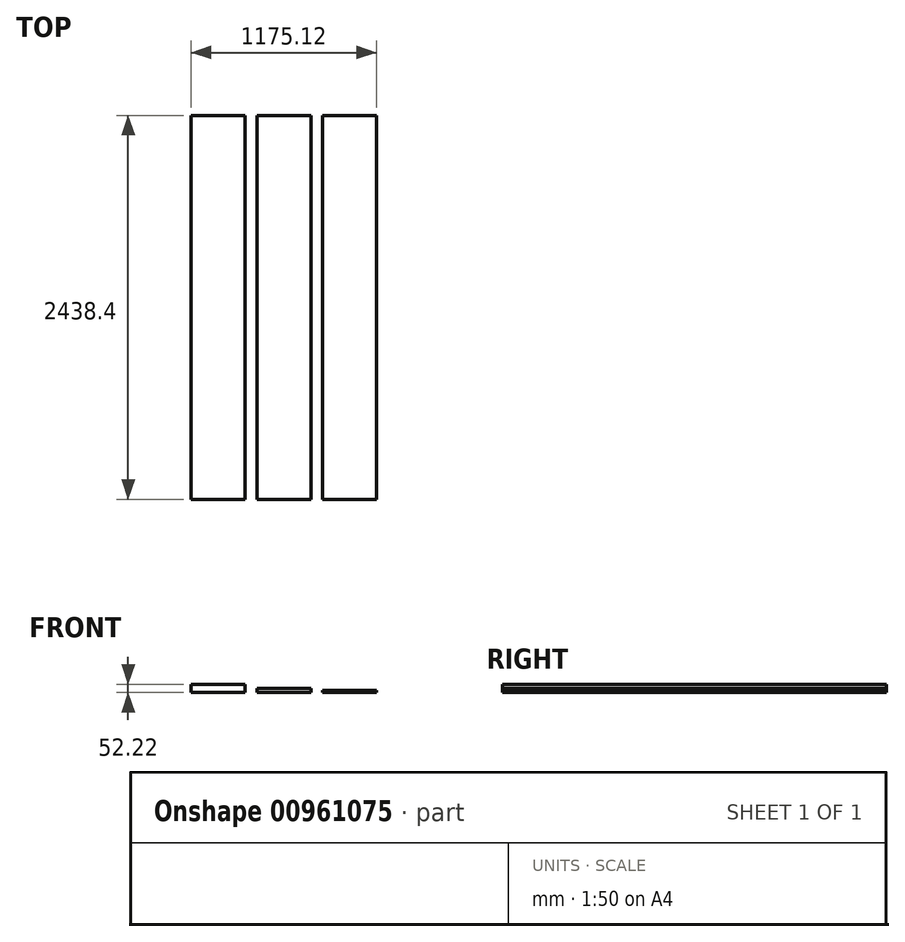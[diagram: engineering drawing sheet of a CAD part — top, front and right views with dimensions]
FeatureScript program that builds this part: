
annotation { "Feature Type Name" : "Feature", "Feature Type Description" : "" }
export const myFeature = defineFeature(function(context is Context, id is Id, definition is map)
    precondition{}
    {
        {
            var Q0;
            Q0=qCreatedBy(makeId("Front.planeOp"),FACE);
            var sketch = newSketch(context, id + "F0", { "sketchPlane" : qUnion([Q0])});
            skLineSegment(sketch, "E0.bottom", {"start": v(-511.36, 64.48) * mm, "end": v(-168.46, 64.48) * mm});
            skLineSegment(sketch, "E0.top", {"start": v(-511.36, 13.68) * mm, "end": v(-168.46, 13.68) * mm});
            skLineSegment(sketch, "E0.left", {"start": v(-511.36, 64.48) * mm, "end": v(-511.36, 13.68) * mm});
            skLineSegment(sketch, "E0.right", {"start": v(-168.46, 64.48) * mm, "end": v(-168.46, 13.68) * mm});
            skLineSegment(sketch, "E1.bottom", {"start": v(-94.85, 37.66) * mm, "end": v(248.05, 37.66) * mm});
            skLineSegment(sketch, "E1.top", {"start": v(-94.85, 12.26) * mm, "end": v(248.05, 12.26) * mm});
            skLineSegment(sketch, "E1.left", {"start": v(-94.85, 37.66) * mm, "end": v(-94.85, 12.26) * mm});
            skLineSegment(sketch, "E1.right", {"start": v(248.05, 37.66) * mm, "end": v(248.05, 12.26) * mm});
            skLineSegment(sketch, "E2.bottom", {"start": v(320.86, 26.07) * mm, "end": v(663.76, 26.07) * mm});
            skLineSegment(sketch, "E2.top", {"start": v(320.86, 13.37) * mm, "end": v(663.76, 13.37) * mm});
            skLineSegment(sketch, "E2.left", {"start": v(320.86, 26.07) * mm, "end": v(320.86, 13.37) * mm});
            skLineSegment(sketch, "E2.right", {"start": v(663.76, 26.07) * mm, "end": v(663.76, 13.37) * mm});
            skSolve(sketch);
        }
        {
            var Q0;
            Q0=makeQuery(id+"F0.imprint","IMPRINT",FACE,{"disambiguationData":[TD([[makeQuery(id+"F0.imprint","IMPRINT",EDGE,{"derivedFrom":sQuery(id+"F0.wireOp",EDGE,"E0.bottom")}),-1.0]])]});
            extrude(context, id + "F1", {"entities" : qUnion([Q0]), "depth" : 2438.4 * mm, "offsetDistance" : 25.4 * mm});
        }
        {
            var Q0;
            Q0=makeQuery(id+"F0.imprint","IMPRINT",FACE,{"disambiguationData":[TD([[makeQuery(id+"F0.imprint","IMPRINT",EDGE,{"derivedFrom":sQuery(id+"F0.wireOp",EDGE,"E1.bottom")}),-1.0]])]});
            extrude(context, id + "F2", {"entities" : qUnion([Q0]), "depth" : 2438.4 * mm, "offsetDistance" : 25.4 * mm});
        }
        {
            var Q0;
            Q0=makeQuery(id+"F0.imprint","IMPRINT",FACE,{"disambiguationData":[TD([[makeQuery(id+"F0.imprint","IMPRINT",EDGE,{"derivedFrom":sQuery(id+"F0.wireOp",EDGE,"E2.bottom")}),-1.0]])]});
            var Q1;
            Q1=sQuery(id+"F0.wireOp",EDGE,"E2.bottom");
            var Q2;
            Q2=sQuery(id+"F0.wireOp",EDGE,"E2.top");
            extrude(context, id + "F3", {"entities" : qUnion([Q0]), "surfaceEntities" : qUnion([Q1, Q2]), "depth" : 2438.4 * mm, "offsetDistance" : 25.4 * mm});
        }
    });
